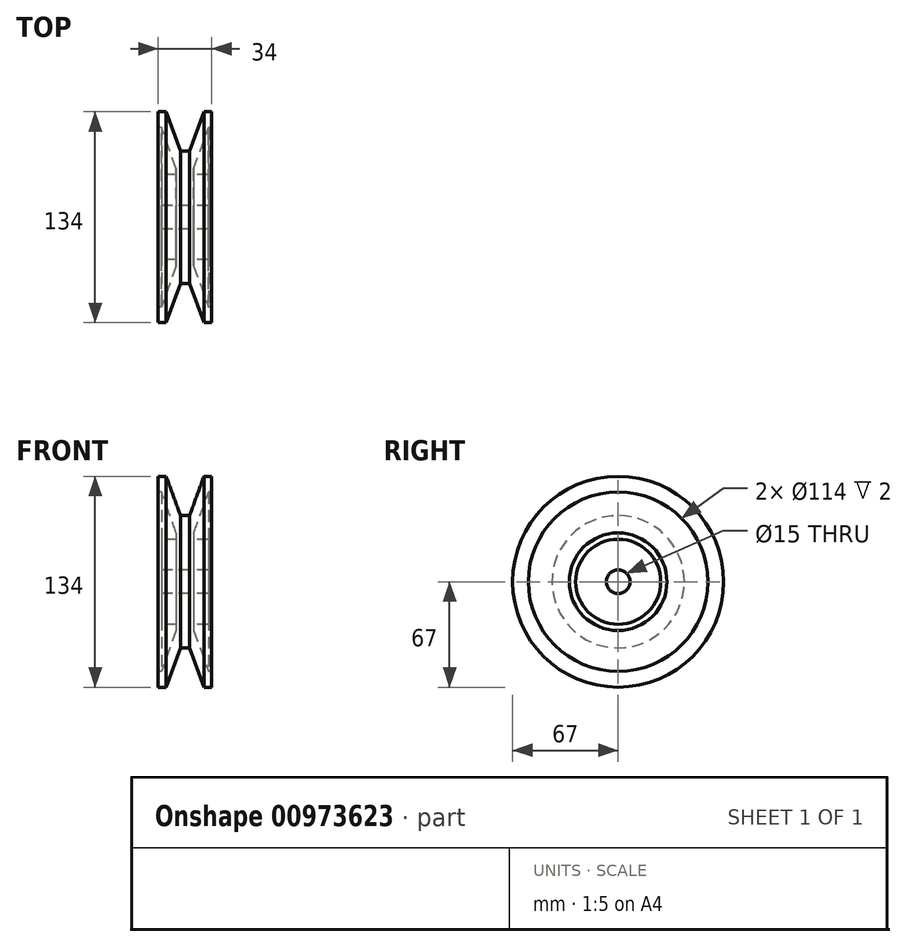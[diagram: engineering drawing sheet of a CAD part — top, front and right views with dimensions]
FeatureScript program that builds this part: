
annotation { "Feature Type Name" : "Feature", "Feature Type Description" : "" }
export const myFeature = defineFeature(function(context is Context, id is Id, definition is map)
    precondition{}
    {
        {
            var Q0;
            Q0=qCreatedBy(makeId("Front.planeOp"),FACE);
            var sketch = newSketch(context, id + "F0", { "sketchPlane" : qUnion([Q0])});
            skLineSegment(sketch, "E0", {"start": v(0, 62.26) * mm, "end": v(0, -60.58) * mm, "construction": true});
            skLineSegment(sketch, "E1", {"start": v(-33.45, 0) * mm, "end": v(36.67, 0) * mm, "construction": true});
            skLineSegment(sketch, "E2", {"start": v(0, 7.5) * mm, "end": v(15, 7.5) * mm});
            skLineSegment(sketch, "E3", {"start": v(15, 27) * mm, "end": v(5.54, 27) * mm});
            skLineSegment(sketch, "E4", {"start": v(5.54, 27) * mm, "end": v(5.54, 31) * mm});
            skLineSegment(sketch, "E5", {"start": v(5.54, 31) * mm, "end": v(15, 57) * mm});
            skLineSegment(sketch, "E6", {"start": v(15, 57) * mm, "end": v(17, 57) * mm});
            skLineSegment(sketch, "E7", {"start": v(17, 57) * mm, "end": v(17, 67) * mm});
            skLineSegment(sketch, "E8", {"start": v(17, 67) * mm, "end": v(12, 67) * mm});
            skLineSegment(sketch, "E9", {"start": v(12, 67) * mm, "end": v(2.9, 42) * mm});
            skLineSegment(sketch, "E10", {"start": v(2.9, 42) * mm, "end": v(0, 42) * mm});
            skLineSegment(sketch, "E11.MirrorCS", {"start": v(-5.54, 27) * mm, "end": v(-5.54, 31) * mm});
            skLineSegment(sketch, "E12.MirrorCS", {"start": v(-2.9, 42) * mm, "end": v(0, 42) * mm});
            skLineSegment(sketch, "E13.MirrorCS", {"start": v(0, 7.5) * mm, "end": v(-15, 7.5) * mm});
            skLineSegment(sketch, "E14.MirrorCS", {"start": v(-5.54, 31) * mm, "end": v(-15, 57) * mm});
            skLineSegment(sketch, "E15.MirrorCS", {"start": v(-17, 57) * mm, "end": v(-17, 67) * mm});
            skLineSegment(sketch, "E16.MirrorCS", {"start": v(-12, 67) * mm, "end": v(-2.9, 42) * mm});
            skLineSegment(sketch, "E17.MirrorCS", {"start": v(-15, 27) * mm, "end": v(-5.54, 27) * mm});
            skLineSegment(sketch, "E18.MirrorCS", {"start": v(-15, 57) * mm, "end": v(-17, 57) * mm});
            skLineSegment(sketch, "E19.MirrorCS", {"start": v(-17, 67) * mm, "end": v(-12, 67) * mm});
            skLineSegment(sketch, "E20", {"start": v(15, 27) * mm, "end": v(15, 7.5) * mm});
            skLineSegment(sketch, "E21.MirrorCS", {"start": v(-15, 27) * mm, "end": v(-15, 7.5) * mm});
            skSolve(sketch);
        }
        {
            var Q0;
            Q0=makeQuery(id+"F0.imprint","IMPRINT",FACE,{"disambiguationData":[TD([[makeQuery(id+"F0.imprint","IMPRINT",EDGE,{"derivedFrom":sQuery(id+"F0.wireOp",EDGE,"0JUGt60Y-3upF-oJ1A-mO7N-oPkKuEYvCSfh")}),-1.0]])]});
            var Q1;
            Q1=makeQuery(id+"F0.imprint","IMPRINT",FACE,{"disambiguationData":[TD([[makeQuery(id+"F0.imprint","IMPRINT",EDGE,{"derivedFrom":sQuery(id+"F0.wireOp",EDGE,"E2")}),1.0]])]});
            var Q2;
            Q2=sQuery(id+"F0.wireOp",EDGE,"E1");
            revolve(context, id + "F1", {"surfaceOperationType" : NewSurfaceOperationType.NEW, "entities" : qUnion([Q0, Q1]), "axis" : qUnion([Q2]), "revolveType" : RevolveType.FULL});
        }
    });
